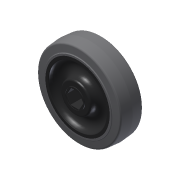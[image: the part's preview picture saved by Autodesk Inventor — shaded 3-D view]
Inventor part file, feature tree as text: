
AUTODESK INVENTOR PART (.ipt)
format: ipt  version: 2015 (Build 190159000, 159)  size: 311,296 bytes
history: native  units: in
note: dims shown in document units (in); Inventor stores cm internally (conversion verified against a paired STEP export)
features: revolve x1, other x1, imported_body x1
ambient origin geometry x8: Origin, YZ Plane, XZ Plane, XY Plane, X Axis, Y Axis, Z Axis, Center Point
bodies: Body1 (feature_tree)
feature tree (3):
  revolve  "Revolve1"  [1 undecoded]
  other  "217-4047-STEP-201410301"
  imported_body  "Base1"
note: 1 required parameter value undecoded (feature->parameter linkage not recoverable at this tier; creation-order binding heuristic only, values carry confidence <= 0.55)
